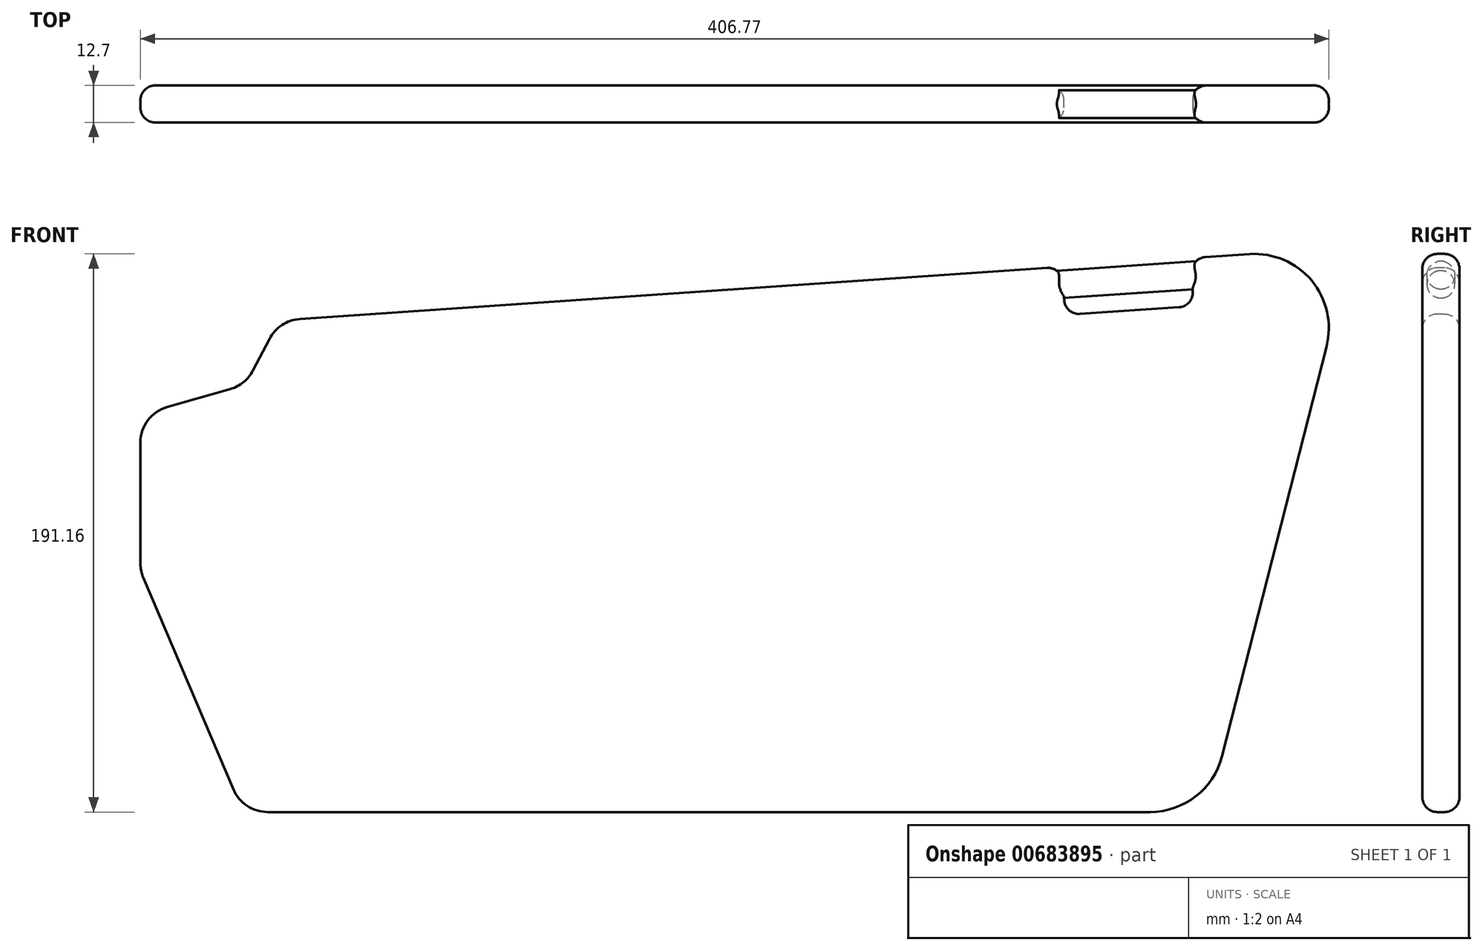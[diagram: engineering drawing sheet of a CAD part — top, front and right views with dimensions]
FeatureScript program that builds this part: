
annotation { "Feature Type Name" : "Feature", "Feature Type Description" : "" }
export const myFeature = defineFeature(function(context is Context, id is Id, definition is map)
    precondition{}
    {
        {
            var Q0;
            Q0=qCreatedBy(makeId("Front.planeOp"),FACE);
            var sketch = newSketch(context, id + "F0", { "sketchPlane" : qUnion([Q0])});
            skLineSegment(sketch, "E0.top", {"start": v(-172.2, -96.75) * mm, "end": v(138.31, -96.75) * mm});
            skLineSegment(sketch, "E0.left", {"start": v(-207.32, 39.4) * mm, "end": v(-207.32, -14.2) * mm});
            skPoint(sketch, "E0.middle", {"position": v(0, 0) * mm});
            skLineSegment(sketch, "E1", {"start": v(198.66, 62.74) * mm, "end": v(162.93, -77.62) * mm});
            skPoint(sketch, "E2.orphan", {"position": v(207.32, -96.75) * mm});
            skLineSegment(sketch, "E3", {"start": v(172.31, 94.35) * mm, "end": v(152.12, 92.97) * mm});
            skPoint(sketch, "E4.orphan", {"position": v(-207.32, 96.75) * mm});
            skLineSegment(sketch, "E5", {"start": v(-207.32, -14.2) * mm, "end": v(-172.2, -96.75) * mm});
            skLineSegment(sketch, "E6", {"start": v(-171.34, 49.6) * mm, "end": v(-207.32, 39.4) * mm});
            skLineSegment(sketch, "E7", {"start": v(108.1, 89.95) * mm, "end": v(109.23, 73.48) * mm});
            skLineSegment(sketch, "E8", {"start": v(109.23, 73.48) * mm, "end": v(153.25, 76.5) * mm});
            skLineSegment(sketch, "E9", {"start": v(153.25, 76.5) * mm, "end": v(152.12, 92.97) * mm});
            skPoint(sketch, "E10.visualSharp", {"position": v(207.32, 96.75) * mm});
            skArc(sketch, "E10.filletArc", {"start": v(198.66, 62.74) * mm, "mid": v(193.56, 85.28) * mm, "end": v(172.31, 94.35) * mm});
            skPoint(sketch, "E11.visualSharp", {"position": v(158.06, -96.75) * mm});
            skArc(sketch, "E11.filletArc", {"start": v(138.31, -96.75) * mm, "mid": v(153.9, -91.4) * mm, "end": v(162.93, -77.62) * mm});
            skPoint(sketch, "E12.orphan", {"position": v(-207.32, 68.35) * mm});
            skPoint(sketch, "E13.orphan", {"position": v(-207.32, -96.75) * mm});
            skLineSegment(sketch, "E14.trimOffspring", {"start": v(108.1, 89.95) * mm, "end": v(-159.88, 71.6) * mm});
            skLineSegment(sketch, "E15", {"start": v(-171.34, 49.6) * mm, "end": v(-159.88, 71.6) * mm});
            skSolve(sketch);
        }
        {
            var Q0;
            Q0=makeQuery(id+"F0.imprint","IMPRINT",FACE,{"disambiguationData":[TD([[makeQuery(id+"F0.imprint","IMPRINT",EDGE,{"derivedFrom":sQuery(id+"F0.wireOp",EDGE,"E0.top")}),1.0]])]});
            extrude(context, id + "F1", {"entities" : qUnion([Q0]), "endBound" : BoundingType.SYMMETRIC, "depth" : 12.7 * mm, "offsetDistance" : 25.4 * mm});
        }
        {
            var Q0;
            Q0=makeQuery(id+"F1.opExtrude","SWEPT_EDGE",EDGE,{"disambiguationData":[OSD([sQuery(id+"F0.wireOp",EDGE,"E6"),sQuery(id+"F0.wireOp",EDGE,"E15")])]});
            var Q1;
            Q1=makeQuery(id+"F1.opExtrude","SWEPT_EDGE",EDGE,{"disambiguationData":[OSD([sQuery(id+"F0.wireOp",EDGE,"E0.left"),sQuery(id+"F0.wireOp",EDGE,"E6")])]});
            var Q2;
            Q2=makeQuery(id+"F1.opExtrude","SWEPT_EDGE",EDGE,{"disambiguationData":[OSD([sQuery(id+"F0.wireOp",EDGE,"E14.trimOffspring"),sQuery(id+"F0.wireOp",EDGE,"E15")])]});
            var Q3;
            Q3=makeQuery(id+"F1.opExtrude","SWEPT_EDGE",EDGE,{"disambiguationData":[OSD([sQuery(id+"F0.wireOp",EDGE,"E0.left"),sQuery(id+"F0.wireOp",EDGE,"E5")])]});
            var Q4;
            Q4=makeQuery(id+"F1.opExtrude","SWEPT_EDGE",EDGE,{"disambiguationData":[OSD([sQuery(id+"F0.wireOp",EDGE,"E0.top"),sQuery(id+"F0.wireOp",EDGE,"E5")])]});
            fillet(context, id + "F2", {"entities" : qUnion([Q0, Q1, Q2, Q3, Q4]), "radius" : 12.7 * mm, "tangentPropagation" : true, "allowEdgeOverflow" : false});
        }
        {
            var Q0;
            Q0=makeQuery(id+"F1.opExtrude","SWEPT_EDGE",EDGE,{"disambiguationData":[OSD([sQuery(id+"F0.wireOp",EDGE,"E7"),sQuery(id+"F0.wireOp",EDGE,"E8")])]});
            var Q1;
            Q1=makeQuery(id+"F1.opExtrude","SWEPT_EDGE",EDGE,{"disambiguationData":[OSD([sQuery(id+"F0.wireOp",EDGE,"E8"),sQuery(id+"F0.wireOp",EDGE,"E9")])]});
            var Q2;
            Q2=makeQuery(id+"F1.opExtrude","SWEPT_EDGE",EDGE,{"disambiguationData":[OSD([sQuery(id+"F0.wireOp",EDGE,"E7"),sQuery(id+"F0.wireOp",EDGE,"E14.trimOffspring")])]});
            var Q3;
            Q3=makeQuery(id+"F1.opExtrude","SWEPT_EDGE",EDGE,{"disambiguationData":[OSD([sQuery(id+"F0.wireOp",EDGE,"E3"),sQuery(id+"F0.wireOp",EDGE,"E9")])]});
            fillet(context, id + "F3", {"entities" : qUnion([Q0, Q1, Q2, Q3]), "radius" : 5.08 * mm, "tangentPropagation" : true, "allowEdgeOverflow" : false});
        }
        {
            var Q0;
            Q0=makeQuery(id+"F1.opExtrude","SWEPT_FACE",FACE,{"disambiguationData":[OSD([sQuery(id+"F0.wireOp",EDGE,"E7")])]});
            var sketch = newSketch(context, id + "F4", { "sketchPlane" : qUnion([Q0])});
            skCircle(sketch, "E16", {"center": v(0, 76.43) * mm, "radius": 4.76 * mm});
            skSolve(sketch);
        }
        {
            var Q0;
            {var subQ0=sQuery(id+"F4.wireOp",EDGE,"E16");var subQ1=sQuery(id+"F0.wireOp",EDGE,"E7");var subQ2=makeQuery(id+"F3.opFillet","BLEND_EDGE",EDGE,{"blendedFrom":[makeQuery(id+"F1.opExtrude","SWEPT_EDGE",EDGE,{"disambiguationData":[OSD([subQ1,sQuery(id+"F0.wireOp",EDGE,"E8")])]}),makeQuery(id+"F1.opExtrude","SWEPT_FACE",FACE,{"disambiguationData":[OSD([subQ1])]})],"blendedInto":[makeQuery(id+"F1.opExtrude","SWEPT_FACE",FACE,{"disambiguationData":[OSD([subQ1])]})]});var subQ3=makeQuery(id+"F4.imprint","INTERSECT",VERTEX,{"disambiguationData":[OD(0.0)],"derivedFrom":[subQ2,subQ0]});Q0=makeQuery(id+"F4.imprint","IMPRINT",FACE,{"disambiguationData":[TD([[makeQuery(id+"F4.imprint","IMPRINT",EDGE,{"disambiguationData":[TD([[subQ3,-1.0]])],"derivedFrom":subQ0}),1.0]])]});}
            var Q1;
            {var subQ0=sQuery(id+"F4.wireOp",EDGE,"E16");var subQ1=sQuery(id+"F0.wireOp",EDGE,"E7");var subQ2=makeQuery(id+"F1.opExtrude","SWEPT_FACE",FACE,{"disambiguationData":[OSD([subQ1])]});var subQ3=makeQuery(id+"F3.opFillet","BLEND_EDGE",EDGE,{"blendedFrom":[makeQuery(id+"F1.opExtrude","SWEPT_EDGE",EDGE,{"disambiguationData":[OSD([subQ1,sQuery(id+"F0.wireOp",EDGE,"E14.trimOffspring")])]}),subQ2],"blendedInto":[subQ2]});var subQ4=makeQuery(id+"F4.imprint","INTERSECT",VERTEX,{"disambiguationData":[OD(0.0)],"derivedFrom":[subQ3,subQ0]});Q1=makeQuery(id+"F4.imprint","IMPRINT",FACE,{"disambiguationData":[TD([[makeQuery(id+"F4.imprint","IMPRINT",EDGE,{"disambiguationData":[TD([[subQ4,-1.0]])],"derivedFrom":subQ0}),1.0]])]});}
            var Q2;
            {var subQ0=sQuery(id+"F4.wireOp",EDGE,"E16");var subQ1=sQuery(id+"F0.wireOp",EDGE,"E7");var subQ2=makeQuery(id+"F3.opFillet","BLEND_EDGE",EDGE,{"blendedFrom":[makeQuery(id+"F1.opExtrude","SWEPT_EDGE",EDGE,{"disambiguationData":[OSD([subQ1,sQuery(id+"F0.wireOp",EDGE,"E14.trimOffspring")])]}),makeQuery(id+"F1.opExtrude","SWEPT_FACE",FACE,{"disambiguationData":[OSD([subQ1])]})],"blendedInto":[makeQuery(id+"F1.opExtrude","SWEPT_FACE",FACE,{"disambiguationData":[OSD([subQ1])]})]});var subQ3=makeQuery(id+"F4.imprint","INTERSECT",VERTEX,{"disambiguationData":[OD(0.0)],"derivedFrom":[subQ2,subQ0]});Q2=makeQuery(id+"F4.imprint","IMPRINT",FACE,{"disambiguationData":[TD([[makeQuery(id+"F4.imprint","IMPRINT",EDGE,{"disambiguationData":[TD([[subQ3,1.0]])],"derivedFrom":subQ0}),1.0]])]});}
            extrude(context, id + "F5", {"entities" : qUnion([Q0, Q1, Q2]), "operationType" : NewBodyOperationType.ADD, "depth" : 50.8 * mm, "offsetDistance" : 25.4 * mm});
        }
        {
            var Q0;
            Q0=makeQuery(id+"F5.opExtrude","CAP_FACE",FACE,{"disambiguationData":[OSD([sQuery(id+"F4.wireOp",EDGE,"E16")])],"isStart":true});
            extrude(context, id + "F6", {"entities" : qUnion([Q0]), "operationType" : NewBodyOperationType.ADD, "depth" : 25.4 * mm, "offsetDistance" : 25.4 * mm});
        }
        {
            var Q0;
            Q0=makeQuery(id+"F1.opExtrude","CAP_EDGE",EDGE,{"disambiguationData":[OSD([sQuery(id+"F0.wireOp",EDGE,"E14.trimOffspring")])],"isStart":false});
            var Q1;
            Q1=makeQuery(id+"F1.opExtrude","CAP_EDGE",EDGE,{"disambiguationData":[OSD([sQuery(id+"F0.wireOp",EDGE,"E14.trimOffspring")])],"isStart":true});
            fillet(context, id + "F7", {"entities" : qUnion([Q0, Q1]), "radius" : 5.08 * mm, "tangentPropagation" : true, "allowEdgeOverflow" : false});
        }
        {
            var Q0;
            Q0=qCreatedBy(makeId("Right.planeOp"),FACE);
            cPlane(context, id + "F8", {"entities" : qUnion([Q0]), "cplaneType" : CPlaneType.OFFSET, "offset" : 162.3 * mm, "oppositeDirection" : true, "width" : 152.4 * mm, "height" : 152.4 * mm});
        }
    });
